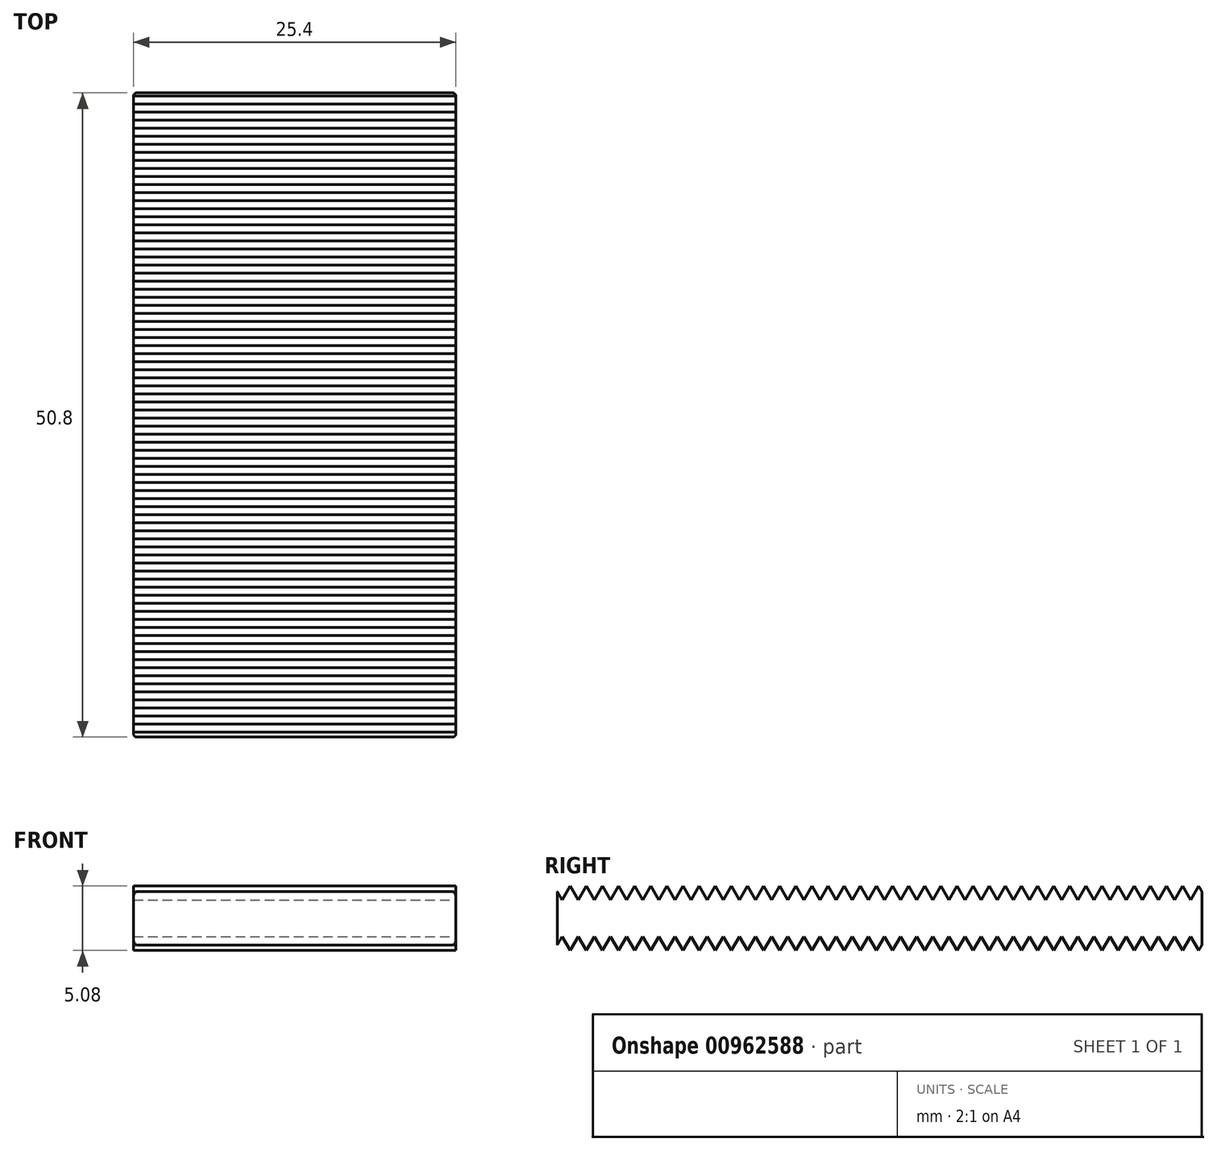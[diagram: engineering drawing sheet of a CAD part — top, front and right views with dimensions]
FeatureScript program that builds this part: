
annotation { "Feature Type Name" : "Feature", "Feature Type Description" : "" }
export const myFeature = defineFeature(function(context is Context, id is Id, definition is map)
    precondition{}
    {
        {
            var Q0;
            Q0=qCreatedBy(makeId("Front.planeOp"),FACE);
            var sketch = newSketch(context, id + "F0", { "sketchPlane" : qUnion([Q0])});
            skLineSegment(sketch, "E0.bottom", {"start": v(12.7, -2.54) * mm, "end": v(-12.7, -2.54) * mm});
            skLineSegment(sketch, "E0.top", {"start": v(12.7, 2.54) * mm, "end": v(-12.7, 2.54) * mm});
            skLineSegment(sketch, "E0.left", {"start": v(12.7, -2.54) * mm, "end": v(12.7, 2.54) * mm});
            skLineSegment(sketch, "E0.right", {"start": v(-12.7, -2.54) * mm, "end": v(-12.7, 2.54) * mm});
            skPoint(sketch, "E0.middle", {"position": v(0, 0) * mm});
            skSolve(sketch);
        }
        {
            var Q0;
            Q0=qSketchRegion(id+"F0",true);
            extrude(context, id + "F1", {"entities" : qUnion([Q0]), "endBound" : BoundingType.SYMMETRIC, "depth" : 50.8 * mm, "offsetDistance" : 25.4 * mm});
        }
        {
            var Q0;
            Q0=qCreatedBy(makeId("Right.planeOp"),FACE);
            var sketch = newSketch(context, id + "F2", { "sketchPlane" : qUnion([Q0])});
            skLineSegment(sketch, "E1", {"start": v(1.02, -2.54) * mm, "end": v(0.38, -1.44) * mm});
            skLineSegment(sketch, "E2", {"start": v(0.38, -1.44) * mm, "end": v(-0.25, -2.54) * mm});
            skLineSegment(sketch, "E3.1.0.0", {"start": v(2.29, -2.54) * mm, "end": v(1.65, -1.44) * mm});
            skLineSegment(sketch, "E3.1.0.1", {"start": v(1.65, -1.44) * mm, "end": v(1.02, -2.54) * mm});
            skLineSegment(sketch, "E3.2.0.0", {"start": v(3.56, -2.54) * mm, "end": v(2.92, -1.44) * mm});
            skLineSegment(sketch, "E3.2.0.1", {"start": v(2.92, -1.44) * mm, "end": v(2.29, -2.54) * mm});
            skLineSegment(sketch, "E3.3.0.0", {"start": v(4.83, -2.54) * mm, "end": v(4.2, -1.44) * mm});
            skLineSegment(sketch, "E3.3.0.1", {"start": v(4.2, -1.44) * mm, "end": v(3.56, -2.54) * mm});
            skLineSegment(sketch, "E3.4.0.0", {"start": v(6.1, -2.54) * mm, "end": v(5.46, -1.44) * mm});
            skLineSegment(sketch, "E3.4.0.1", {"start": v(5.46, -1.44) * mm, "end": v(4.83, -2.54) * mm});
            skLineSegment(sketch, "E3.5.0.0", {"start": v(7.37, -2.54) * mm, "end": v(6.73, -1.44) * mm});
            skLineSegment(sketch, "E3.5.0.1", {"start": v(6.73, -1.44) * mm, "end": v(6.1, -2.54) * mm});
            skLineSegment(sketch, "E3.6.0.0", {"start": v(8.64, -2.54) * mm, "end": v(8, -1.44) * mm});
            skLineSegment(sketch, "E3.6.0.1", {"start": v(8, -1.44) * mm, "end": v(7.37, -2.54) * mm});
            skLineSegment(sketch, "E3.7.0.0", {"start": v(9.9, -2.54) * mm, "end": v(9.27, -1.44) * mm});
            skLineSegment(sketch, "E3.7.0.1", {"start": v(9.27, -1.44) * mm, "end": v(8.64, -2.54) * mm});
            skLineSegment(sketch, "E3.8.0.0", {"start": v(11.18, -2.54) * mm, "end": v(10.54, -1.44) * mm});
            skLineSegment(sketch, "E3.8.0.1", {"start": v(10.54, -1.44) * mm, "end": v(9.9, -2.54) * mm});
            skLineSegment(sketch, "E3.9.0.0", {"start": v(12.45, -2.54) * mm, "end": v(11.81, -1.44) * mm});
            skLineSegment(sketch, "E3.9.0.1", {"start": v(11.81, -1.44) * mm, "end": v(11.18, -2.54) * mm});
            skLineSegment(sketch, "E3.10.0.0", {"start": v(13.72, -2.54) * mm, "end": v(13.08, -1.44) * mm});
            skLineSegment(sketch, "E3.10.0.1", {"start": v(13.08, -1.44) * mm, "end": v(12.45, -2.54) * mm});
            skLineSegment(sketch, "E3.11.0.0", {"start": v(14.99, -2.54) * mm, "end": v(14.35, -1.44) * mm});
            skLineSegment(sketch, "E3.11.0.1", {"start": v(14.35, -1.44) * mm, "end": v(13.72, -2.54) * mm});
            skLineSegment(sketch, "E3.12.0.0", {"start": v(16.26, -2.54) * mm, "end": v(15.62, -1.44) * mm});
            skLineSegment(sketch, "E3.12.0.1", {"start": v(15.62, -1.44) * mm, "end": v(14.99, -2.54) * mm});
            skLineSegment(sketch, "E3.13.0.0", {"start": v(17.53, -2.54) * mm, "end": v(16.9, -1.44) * mm});
            skLineSegment(sketch, "E3.13.0.1", {"start": v(16.9, -1.44) * mm, "end": v(16.26, -2.54) * mm});
            skLineSegment(sketch, "E3.14.0.0", {"start": v(18.8, -2.54) * mm, "end": v(18.16, -1.44) * mm});
            skLineSegment(sketch, "E3.14.0.1", {"start": v(18.16, -1.44) * mm, "end": v(17.53, -2.54) * mm});
            skLineSegment(sketch, "E3.15.0.0", {"start": v(20.07, -2.54) * mm, "end": v(19.43, -1.44) * mm});
            skLineSegment(sketch, "E3.15.0.1", {"start": v(19.43, -1.44) * mm, "end": v(18.8, -2.54) * mm});
            skLineSegment(sketch, "E3.16.0.0", {"start": v(21.34, -2.54) * mm, "end": v(20.7, -1.44) * mm});
            skLineSegment(sketch, "E3.16.0.1", {"start": v(20.7, -1.44) * mm, "end": v(20.07, -2.54) * mm});
            skLineSegment(sketch, "E3.17.0.0", {"start": v(22.6, -2.54) * mm, "end": v(21.97, -1.44) * mm});
            skLineSegment(sketch, "E3.17.0.1", {"start": v(21.97, -1.44) * mm, "end": v(21.34, -2.54) * mm});
            skLineSegment(sketch, "E3.18.0.0", {"start": v(23.88, -2.54) * mm, "end": v(23.24, -1.44) * mm});
            skLineSegment(sketch, "E3.18.0.1", {"start": v(23.24, -1.44) * mm, "end": v(22.6, -2.54) * mm});
            skLineSegment(sketch, "E3.19.0.0", {"start": v(25.15, -2.54) * mm, "end": v(24.51, -1.44) * mm});
            skLineSegment(sketch, "E3.19.0.1", {"start": v(24.51, -1.44) * mm, "end": v(23.88, -2.54) * mm});
            skLineSegment(sketch, "E3.20.0.0", {"start": v(26.42, -2.54) * mm, "end": v(25.78, -1.44) * mm});
            skLineSegment(sketch, "E3.20.0.1", {"start": v(25.78, -1.44) * mm, "end": v(25.15, -2.54) * mm});
            skLineSegment(sketch, "E3.21.0.0", {"start": v(27.69, -2.54) * mm, "end": v(27.05, -1.44) * mm});
            skLineSegment(sketch, "E3.21.0.1", {"start": v(27.05, -1.44) * mm, "end": v(26.42, -2.54) * mm});
            skLineSegment(sketch, "E3.22.0.0", {"start": v(28.96, -2.54) * mm, "end": v(28.32, -1.44) * mm});
            skLineSegment(sketch, "E3.22.0.1", {"start": v(28.32, -1.44) * mm, "end": v(27.69, -2.54) * mm});
            skLineSegment(sketch, "E3.23.0.0", {"start": v(30.23, -2.54) * mm, "end": v(29.6, -1.44) * mm});
            skLineSegment(sketch, "E3.23.0.1", {"start": v(29.6, -1.44) * mm, "end": v(28.96, -2.54) * mm});
            skLineSegment(sketch, "E3.24.0.0", {"start": v(31.5, -2.54) * mm, "end": v(30.86, -1.44) * mm});
            skLineSegment(sketch, "E3.24.0.1", {"start": v(30.86, -1.44) * mm, "end": v(30.23, -2.54) * mm});
            skLineSegment(sketch, "E3.direction1", {"start": v(-0.25, -2.54) * mm, "end": v(1.02, -2.54) * mm, "construction": true});
            skLineSegment(sketch, "E4.1.0.0", {"start": v(-0.25, -2.54) * mm, "end": v(-0.89, -1.44) * mm});
            skLineSegment(sketch, "E4.1.0.1", {"start": v(-0.89, -1.44) * mm, "end": v(-1.52, -2.54) * mm});
            skLineSegment(sketch, "E4.2.0.0", {"start": v(-1.52, -2.54) * mm, "end": v(-2.16, -1.44) * mm});
            skLineSegment(sketch, "E4.2.0.1", {"start": v(-2.16, -1.44) * mm, "end": v(-2.8, -2.54) * mm});
            skLineSegment(sketch, "E4.3.0.0", {"start": v(-2.8, -2.54) * mm, "end": v(-3.43, -1.44) * mm});
            skLineSegment(sketch, "E4.3.0.1", {"start": v(-3.43, -1.44) * mm, "end": v(-4.06, -2.54) * mm});
            skLineSegment(sketch, "E4.4.0.0", {"start": v(-4.06, -2.54) * mm, "end": v(-4.7, -1.44) * mm});
            skLineSegment(sketch, "E4.4.0.1", {"start": v(-4.7, -1.44) * mm, "end": v(-5.33, -2.54) * mm});
            skLineSegment(sketch, "E4.5.0.0", {"start": v(-5.33, -2.54) * mm, "end": v(-5.97, -1.44) * mm});
            skLineSegment(sketch, "E4.5.0.1", {"start": v(-5.97, -1.44) * mm, "end": v(-6.6, -2.54) * mm});
            skLineSegment(sketch, "E4.6.0.0", {"start": v(-6.6, -2.54) * mm, "end": v(-7.24, -1.44) * mm});
            skLineSegment(sketch, "E4.6.0.1", {"start": v(-7.24, -1.44) * mm, "end": v(-7.87, -2.54) * mm});
            skLineSegment(sketch, "E4.7.0.0", {"start": v(-7.87, -2.54) * mm, "end": v(-8.5, -1.44) * mm});
            skLineSegment(sketch, "E4.7.0.1", {"start": v(-8.5, -1.44) * mm, "end": v(-9.14, -2.54) * mm});
            skLineSegment(sketch, "E4.8.0.0", {"start": v(-9.14, -2.54) * mm, "end": v(-9.78, -1.44) * mm});
            skLineSegment(sketch, "E4.8.0.1", {"start": v(-9.78, -1.44) * mm, "end": v(-10.41, -2.54) * mm});
            skLineSegment(sketch, "E4.9.0.0", {"start": v(-10.41, -2.54) * mm, "end": v(-11.05, -1.44) * mm});
            skLineSegment(sketch, "E4.9.0.1", {"start": v(-11.05, -1.44) * mm, "end": v(-11.68, -2.54) * mm});
            skLineSegment(sketch, "E4.10.0.0", {"start": v(-11.68, -2.54) * mm, "end": v(-12.32, -1.44) * mm});
            skLineSegment(sketch, "E4.10.0.1", {"start": v(-12.32, -1.44) * mm, "end": v(-12.95, -2.54) * mm});
            skLineSegment(sketch, "E4.11.0.0", {"start": v(-12.95, -2.54) * mm, "end": v(-13.59, -1.44) * mm});
            skLineSegment(sketch, "E4.11.0.1", {"start": v(-13.59, -1.44) * mm, "end": v(-14.22, -2.54) * mm});
            skLineSegment(sketch, "E4.12.0.0", {"start": v(-14.22, -2.54) * mm, "end": v(-14.86, -1.44) * mm});
            skLineSegment(sketch, "E4.12.0.1", {"start": v(-14.86, -1.44) * mm, "end": v(-15.5, -2.54) * mm});
            skLineSegment(sketch, "E4.13.0.0", {"start": v(-15.5, -2.54) * mm, "end": v(-16.13, -1.44) * mm});
            skLineSegment(sketch, "E4.13.0.1", {"start": v(-16.13, -1.44) * mm, "end": v(-16.76, -2.54) * mm});
            skLineSegment(sketch, "E4.14.0.0", {"start": v(-16.76, -2.54) * mm, "end": v(-17.4, -1.44) * mm});
            skLineSegment(sketch, "E4.14.0.1", {"start": v(-17.4, -1.44) * mm, "end": v(-18.03, -2.54) * mm});
            skLineSegment(sketch, "E4.15.0.0", {"start": v(-18.03, -2.54) * mm, "end": v(-18.67, -1.44) * mm});
            skLineSegment(sketch, "E4.15.0.1", {"start": v(-18.67, -1.44) * mm, "end": v(-19.3, -2.54) * mm});
            skLineSegment(sketch, "E4.16.0.0", {"start": v(-19.3, -2.54) * mm, "end": v(-19.94, -1.44) * mm});
            skLineSegment(sketch, "E4.16.0.1", {"start": v(-19.94, -1.44) * mm, "end": v(-20.57, -2.54) * mm});
            skLineSegment(sketch, "E4.17.0.0", {"start": v(-20.57, -2.54) * mm, "end": v(-21.2, -1.44) * mm});
            skLineSegment(sketch, "E4.17.0.1", {"start": v(-21.2, -1.44) * mm, "end": v(-21.84, -2.54) * mm});
            skLineSegment(sketch, "E4.18.0.0", {"start": v(-21.84, -2.54) * mm, "end": v(-22.48, -1.44) * mm});
            skLineSegment(sketch, "E4.18.0.1", {"start": v(-22.48, -1.44) * mm, "end": v(-23.11, -2.54) * mm});
            skLineSegment(sketch, "E4.19.0.0", {"start": v(-23.11, -2.54) * mm, "end": v(-23.75, -1.44) * mm});
            skLineSegment(sketch, "E4.19.0.1", {"start": v(-23.75, -1.44) * mm, "end": v(-24.38, -2.54) * mm});
            skLineSegment(sketch, "E4.20.0.0", {"start": v(-24.38, -2.54) * mm, "end": v(-25.02, -1.44) * mm});
            skLineSegment(sketch, "E4.20.0.1", {"start": v(-25.02, -1.44) * mm, "end": v(-25.65, -2.54) * mm});
            skLineSegment(sketch, "E4.21.0.0", {"start": v(-25.65, -2.54) * mm, "end": v(-26.29, -1.44) * mm});
            skLineSegment(sketch, "E4.21.0.1", {"start": v(-26.29, -1.44) * mm, "end": v(-26.92, -2.54) * mm});
            skLineSegment(sketch, "E4.22.0.0", {"start": v(-26.92, -2.54) * mm, "end": v(-27.56, -1.44) * mm});
            skLineSegment(sketch, "E4.22.0.1", {"start": v(-27.56, -1.44) * mm, "end": v(-28.2, -2.54) * mm});
            skLineSegment(sketch, "E4.23.0.0", {"start": v(-28.2, -2.54) * mm, "end": v(-28.83, -1.44) * mm});
            skLineSegment(sketch, "E4.23.0.1", {"start": v(-28.83, -1.44) * mm, "end": v(-29.46, -2.54) * mm});
            skLineSegment(sketch, "E4.direction1", {"start": v(-0.25, -2.54) * mm, "end": v(-1.52, -2.54) * mm, "construction": true});
            skLineSegment(sketch, "E5", {"start": v(-29.46, -2.54) * mm, "end": v(-29.46, -2.8) * mm});
            skLineSegment(sketch, "E6", {"start": v(-29.46, -2.8) * mm, "end": v(31.5, -2.8) * mm});
            skLineSegment(sketch, "E7", {"start": v(31.5, -2.8) * mm, "end": v(31.5, -2.54) * mm});
            skLineSegment(sketch, "E8.MirrorCS", {"start": v(31.5, 2.8) * mm, "end": v(31.5, 2.54) * mm});
            skLineSegment(sketch, "E9.MirrorCS", {"start": v(-29.46, 2.54) * mm, "end": v(-29.46, 2.8) * mm});
            skLineSegment(sketch, "E10.MirrorCS", {"start": v(1.02, 2.54) * mm, "end": v(0.38, 1.44) * mm});
            skLineSegment(sketch, "E11.MirrorCS", {"start": v(-0.25, 2.54) * mm, "end": v(1.02, 2.54) * mm, "construction": true});
            skLineSegment(sketch, "E12.MirrorCS", {"start": v(1.65, 1.44) * mm, "end": v(1.02, 2.54) * mm});
            skLineSegment(sketch, "E13.MirrorCS", {"start": v(0.38, 1.44) * mm, "end": v(-0.25, 2.54) * mm});
            skLineSegment(sketch, "E14.MirrorCS", {"start": v(2.29, 2.54) * mm, "end": v(1.65, 1.44) * mm});
            skLineSegment(sketch, "E15.MirrorCS", {"start": v(-0.89, 1.44) * mm, "end": v(-1.52, 2.54) * mm});
            skLineSegment(sketch, "E16.MirrorCS", {"start": v(-0.25, 2.54) * mm, "end": v(-1.52, 2.54) * mm, "construction": true});
            skLineSegment(sketch, "E17.MirrorCS", {"start": v(-0.25, 2.54) * mm, "end": v(-0.89, 1.44) * mm});
            skLineSegment(sketch, "E18.MirrorCS", {"start": v(29.6, 1.44) * mm, "end": v(28.96, 2.54) * mm});
            skLineSegment(sketch, "E19.MirrorCS", {"start": v(15.62, 1.44) * mm, "end": v(14.99, 2.54) * mm});
            skLineSegment(sketch, "E20.MirrorCS", {"start": v(-26.29, 1.44) * mm, "end": v(-26.92, 2.54) * mm});
            skLineSegment(sketch, "E21.MirrorCS", {"start": v(4.2, 1.44) * mm, "end": v(3.56, 2.54) * mm});
            skLineSegment(sketch, "E22.MirrorCS", {"start": v(-23.11, 2.54) * mm, "end": v(-23.75, 1.44) * mm});
            skLineSegment(sketch, "E23.MirrorCS", {"start": v(-13.59, 1.44) * mm, "end": v(-14.22, 2.54) * mm});
            skLineSegment(sketch, "E24.MirrorCS", {"start": v(12.45, 2.54) * mm, "end": v(11.81, 1.44) * mm});
            skLineSegment(sketch, "E25.MirrorCS", {"start": v(27.05, 1.44) * mm, "end": v(26.42, 2.54) * mm});
            skLineSegment(sketch, "E26.MirrorCS", {"start": v(2.92, 1.44) * mm, "end": v(2.29, 2.54) * mm});
            skLineSegment(sketch, "E27.MirrorCS", {"start": v(-12.32, 1.44) * mm, "end": v(-12.95, 2.54) * mm});
            skLineSegment(sketch, "E28.MirrorCS", {"start": v(-4.7, 1.44) * mm, "end": v(-5.33, 2.54) * mm});
            skLineSegment(sketch, "E29.MirrorCS", {"start": v(-28.83, 1.44) * mm, "end": v(-29.46, 2.54) * mm});
            skLineSegment(sketch, "E30.MirrorCS", {"start": v(9.9, 2.54) * mm, "end": v(9.27, 1.44) * mm});
            skLineSegment(sketch, "E31.MirrorCS", {"start": v(-17.4, 1.44) * mm, "end": v(-18.03, 2.54) * mm});
            skLineSegment(sketch, "E32.MirrorCS", {"start": v(6.73, 1.44) * mm, "end": v(6.1, 2.54) * mm});
            skLineSegment(sketch, "E33.MirrorCS", {"start": v(-3.43, 1.44) * mm, "end": v(-4.06, 2.54) * mm});
            skLineSegment(sketch, "E34.MirrorCS", {"start": v(-9.78, 1.44) * mm, "end": v(-10.41, 2.54) * mm});
            skLineSegment(sketch, "E35.MirrorCS", {"start": v(4.83, 2.54) * mm, "end": v(4.2, 1.44) * mm});
            skLineSegment(sketch, "E36.MirrorCS", {"start": v(-7.24, 1.44) * mm, "end": v(-7.87, 2.54) * mm});
            skLineSegment(sketch, "E37.MirrorCS", {"start": v(-1.52, 2.54) * mm, "end": v(-2.16, 1.44) * mm});
            skLineSegment(sketch, "E38.MirrorCS", {"start": v(-8.5, 1.44) * mm, "end": v(-9.14, 2.54) * mm});
            skLineSegment(sketch, "E39.MirrorCS", {"start": v(-18.67, 1.44) * mm, "end": v(-19.3, 2.54) * mm});
            skLineSegment(sketch, "E40.MirrorCS", {"start": v(8.64, 2.54) * mm, "end": v(8, 1.44) * mm});
            skLineSegment(sketch, "E41.MirrorCS", {"start": v(14.99, 2.54) * mm, "end": v(14.35, 1.44) * mm});
            skLineSegment(sketch, "E42.MirrorCS", {"start": v(-6.6, 2.54) * mm, "end": v(-7.24, 1.44) * mm});
            skLineSegment(sketch, "E43.MirrorCS", {"start": v(-12.95, 2.54) * mm, "end": v(-13.59, 1.44) * mm});
            skLineSegment(sketch, "E44.MirrorCS", {"start": v(31.5, 2.54) * mm, "end": v(30.86, 1.44) * mm});
            skLineSegment(sketch, "E45.MirrorCS", {"start": v(20.7, 1.44) * mm, "end": v(20.07, 2.54) * mm});
            skLineSegment(sketch, "E46.MirrorCS", {"start": v(-24.38, 2.54) * mm, "end": v(-25.02, 1.44) * mm});
            skLineSegment(sketch, "E47.MirrorCS", {"start": v(16.9, 1.44) * mm, "end": v(16.26, 2.54) * mm});
            skLineSegment(sketch, "E48.MirrorCS", {"start": v(30.86, 1.44) * mm, "end": v(30.23, 2.54) * mm});
            skLineSegment(sketch, "E49.MirrorCS", {"start": v(-18.03, 2.54) * mm, "end": v(-18.67, 1.44) * mm});
            skLineSegment(sketch, "E50.MirrorCS", {"start": v(-15.5, 2.54) * mm, "end": v(-16.13, 1.44) * mm});
            skLineSegment(sketch, "E51.MirrorCS", {"start": v(13.72, 2.54) * mm, "end": v(13.08, 1.44) * mm});
            skLineSegment(sketch, "E52.MirrorCS", {"start": v(-22.48, 1.44) * mm, "end": v(-23.11, 2.54) * mm});
            skLineSegment(sketch, "E53.MirrorCS", {"start": v(-19.94, 1.44) * mm, "end": v(-20.57, 2.54) * mm});
            skLineSegment(sketch, "E54.MirrorCS", {"start": v(17.53, 2.54) * mm, "end": v(16.9, 1.44) * mm});
            skLineSegment(sketch, "E55.MirrorCS", {"start": v(-9.14, 2.54) * mm, "end": v(-9.78, 1.44) * mm});
            skLineSegment(sketch, "E56.MirrorCS", {"start": v(-10.41, 2.54) * mm, "end": v(-11.05, 1.44) * mm});
            skLineSegment(sketch, "E57.MirrorCS", {"start": v(-16.76, 2.54) * mm, "end": v(-17.4, 1.44) * mm});
            skLineSegment(sketch, "E58.MirrorCS", {"start": v(24.51, 1.44) * mm, "end": v(23.88, 2.54) * mm});
            skLineSegment(sketch, "E59.MirrorCS", {"start": v(13.08, 1.44) * mm, "end": v(12.45, 2.54) * mm});
            skLineSegment(sketch, "E60.MirrorCS", {"start": v(-2.16, 1.44) * mm, "end": v(-2.8, 2.54) * mm});
            skLineSegment(sketch, "E61.MirrorCS", {"start": v(-5.33, 2.54) * mm, "end": v(-5.97, 1.44) * mm});
            skLineSegment(sketch, "E62.MirrorCS", {"start": v(7.37, 2.54) * mm, "end": v(6.73, 1.44) * mm});
            skLineSegment(sketch, "E63.MirrorCS", {"start": v(-27.56, 1.44) * mm, "end": v(-28.2, 2.54) * mm});
            skLineSegment(sketch, "E64.MirrorCS", {"start": v(-23.75, 1.44) * mm, "end": v(-24.38, 2.54) * mm});
            skLineSegment(sketch, "E65.MirrorCS", {"start": v(16.26, 2.54) * mm, "end": v(15.62, 1.44) * mm});
            skLineSegment(sketch, "E66.MirrorCS", {"start": v(6.1, 2.54) * mm, "end": v(5.46, 1.44) * mm});
            skLineSegment(sketch, "E67.MirrorCS", {"start": v(-4.06, 2.54) * mm, "end": v(-4.7, 1.44) * mm});
            skLineSegment(sketch, "E68.MirrorCS", {"start": v(28.32, 1.44) * mm, "end": v(27.69, 2.54) * mm});
            skLineSegment(sketch, "E69.MirrorCS", {"start": v(11.81, 1.44) * mm, "end": v(11.18, 2.54) * mm});
            skLineSegment(sketch, "E70.MirrorCS", {"start": v(-2.8, 2.54) * mm, "end": v(-3.43, 1.44) * mm});
            skLineSegment(sketch, "E71.MirrorCS", {"start": v(-11.05, 1.44) * mm, "end": v(-11.68, 2.54) * mm});
            skLineSegment(sketch, "E72.MirrorCS", {"start": v(18.16, 1.44) * mm, "end": v(17.53, 2.54) * mm});
            skLineSegment(sketch, "E73.MirrorCS", {"start": v(5.46, 1.44) * mm, "end": v(4.83, 2.54) * mm});
            skLineSegment(sketch, "E74.MirrorCS", {"start": v(-16.13, 1.44) * mm, "end": v(-16.76, 2.54) * mm});
            skLineSegment(sketch, "E75.MirrorCS", {"start": v(10.54, 1.44) * mm, "end": v(9.9, 2.54) * mm});
            skLineSegment(sketch, "E76.MirrorCS", {"start": v(11.18, 2.54) * mm, "end": v(10.54, 1.44) * mm});
            skLineSegment(sketch, "E77.MirrorCS", {"start": v(-20.57, 2.54) * mm, "end": v(-21.2, 1.44) * mm});
            skLineSegment(sketch, "E78.MirrorCS", {"start": v(-21.2, 1.44) * mm, "end": v(-21.84, 2.54) * mm});
            skLineSegment(sketch, "E79.MirrorCS", {"start": v(-5.97, 1.44) * mm, "end": v(-6.6, 2.54) * mm});
            skLineSegment(sketch, "E80.MirrorCS", {"start": v(-28.2, 2.54) * mm, "end": v(-28.83, 1.44) * mm});
            skLineSegment(sketch, "E81.MirrorCS", {"start": v(-7.87, 2.54) * mm, "end": v(-8.5, 1.44) * mm});
            skLineSegment(sketch, "E82.MirrorCS", {"start": v(25.15, 2.54) * mm, "end": v(24.51, 1.44) * mm});
            skLineSegment(sketch, "E83.MirrorCS", {"start": v(3.56, 2.54) * mm, "end": v(2.92, 1.44) * mm});
            skLineSegment(sketch, "E84.MirrorCS", {"start": v(9.27, 1.44) * mm, "end": v(8.64, 2.54) * mm});
            skLineSegment(sketch, "E85.MirrorCS", {"start": v(-19.3, 2.54) * mm, "end": v(-19.94, 1.44) * mm});
            skLineSegment(sketch, "E86.MirrorCS", {"start": v(30.23, 2.54) * mm, "end": v(29.6, 1.44) * mm});
            skLineSegment(sketch, "E87.MirrorCS", {"start": v(18.8, 2.54) * mm, "end": v(18.16, 1.44) * mm});
            skLineSegment(sketch, "E88.MirrorCS", {"start": v(-11.68, 2.54) * mm, "end": v(-12.32, 1.44) * mm});
            skLineSegment(sketch, "E89.MirrorCS", {"start": v(21.97, 1.44) * mm, "end": v(21.34, 2.54) * mm});
            skLineSegment(sketch, "E90.MirrorCS", {"start": v(21.34, 2.54) * mm, "end": v(20.7, 1.44) * mm});
            skLineSegment(sketch, "E91.MirrorCS", {"start": v(20.07, 2.54) * mm, "end": v(19.43, 1.44) * mm});
            skLineSegment(sketch, "E92.MirrorCS", {"start": v(-29.46, 2.8) * mm, "end": v(31.5, 2.8) * mm});
            skLineSegment(sketch, "E93.MirrorCS", {"start": v(27.69, 2.54) * mm, "end": v(27.05, 1.44) * mm});
            skLineSegment(sketch, "E94.MirrorCS", {"start": v(-25.65, 2.54) * mm, "end": v(-26.29, 1.44) * mm});
            skLineSegment(sketch, "E95.MirrorCS", {"start": v(-14.22, 2.54) * mm, "end": v(-14.86, 1.44) * mm});
            skLineSegment(sketch, "E96.MirrorCS", {"start": v(-26.92, 2.54) * mm, "end": v(-27.56, 1.44) * mm});
            skLineSegment(sketch, "E97.MirrorCS", {"start": v(23.24, 1.44) * mm, "end": v(22.6, 2.54) * mm});
            skLineSegment(sketch, "E98.MirrorCS", {"start": v(26.42, 2.54) * mm, "end": v(25.78, 1.44) * mm});
            skLineSegment(sketch, "E99.MirrorCS", {"start": v(28.96, 2.54) * mm, "end": v(28.32, 1.44) * mm});
            skLineSegment(sketch, "E100.MirrorCS", {"start": v(19.43, 1.44) * mm, "end": v(18.8, 2.54) * mm});
            skLineSegment(sketch, "E101.MirrorCS", {"start": v(25.78, 1.44) * mm, "end": v(25.15, 2.54) * mm});
            skLineSegment(sketch, "E102.MirrorCS", {"start": v(8, 1.44) * mm, "end": v(7.37, 2.54) * mm});
            skLineSegment(sketch, "E103.MirrorCS", {"start": v(22.6, 2.54) * mm, "end": v(21.97, 1.44) * mm});
            skLineSegment(sketch, "E104.MirrorCS", {"start": v(14.35, 1.44) * mm, "end": v(13.72, 2.54) * mm});
            skLineSegment(sketch, "E105.MirrorCS", {"start": v(-21.84, 2.54) * mm, "end": v(-22.48, 1.44) * mm});
            skLineSegment(sketch, "E106.MirrorCS", {"start": v(-14.86, 1.44) * mm, "end": v(-15.5, 2.54) * mm});
            skLineSegment(sketch, "E107.MirrorCS", {"start": v(-25.02, 1.44) * mm, "end": v(-25.65, 2.54) * mm});
            skLineSegment(sketch, "E108.MirrorCS", {"start": v(23.88, 2.54) * mm, "end": v(23.24, 1.44) * mm});
            skSolve(sketch);
        }
        {
            var Q0;
            Q0=qSketchRegion(id+"F2",true);
            extrude(context, id + "F3", {"entities" : qUnion([Q0]), "operationType" : NewBodyOperationType.REMOVE, "endBound" : BoundingType.SYMMETRIC, "oppositeDirection" : true, "depth" : 25.4 * mm, "offsetDistance" : 25.4 * mm});
        }
        {
            var Q0;
            Q0=makeQuery(id+"F1.opExtrude","CAP_EDGE",EDGE,{"disambiguationData":[OSD([sQuery(id+"F0.wireOp",EDGE,"E0.left")])],"isStart":false});
            var Q1;
            Q1=makeQuery(id+"F1.opExtrude","CAP_EDGE",EDGE,{"disambiguationData":[OSD([sQuery(id+"F0.wireOp",EDGE,"E0.right")])],"isStart":false});
            var Q2;
            Q2=makeQuery(id+"F3.boolean.opBoolean","MERGE",EDGE,{"derivedFrom":[makeQuery(id+"F1.opExtrude","CAP_EDGE",EDGE,{"disambiguationData":[OSD([sQuery(id+"F0.wireOp",EDGE,"E0.top")])],"isStart":false})],"fromTools":[makeQuery(id+"F3.opExtrude","SWEPT_EDGE",EDGE,{"disambiguationData":[OSD([sQuery(id+"F2.wireOp",EDGE,"accb9737-dca4-4821-836c-b98c3f27e90128.MirrorCS"),sQuery(id+"F2.wireOp",EDGE,"accb9737-dca4-4821-836c-b98c3f27e901305.MirrorCS")])]})]});
            var Q3;
            Q3=makeQuery(id+"F3.boolean.opBoolean","MERGE",EDGE,{"derivedFrom":[makeQuery(id+"F1.opExtrude","CAP_EDGE",EDGE,{"disambiguationData":[OSD([sQuery(id+"F0.wireOp",EDGE,"E0.bottom")])],"isStart":false})],"fromTools":[makeQuery(id+"F3.opExtrude","SWEPT_EDGE",EDGE,{"disambiguationData":[OSD([sQuery(id+"F2.wireOp",EDGE,"E4.74.0.1"),sQuery(id+"F2.wireOp",EDGE,"E4.75.0.0")])]})]});
            var Q4;
            Q4=makeQuery(id+"F1.opExtrude","CAP_EDGE",EDGE,{"disambiguationData":[OSD([sQuery(id+"F0.wireOp",EDGE,"E0.right")])],"isStart":true});
            var Q5;
            Q5=makeQuery(id+"F3.boolean.opBoolean","MERGE",EDGE,{"derivedFrom":[makeQuery(id+"F1.opExtrude","CAP_EDGE",EDGE,{"disambiguationData":[OSD([sQuery(id+"F0.wireOp",EDGE,"E0.top")])],"isStart":true})],"fromTools":[makeQuery(id+"F3.opExtrude","SWEPT_EDGE",EDGE,{"disambiguationData":[OSD([sQuery(id+"F2.wireOp",EDGE,"accb9737-dca4-4821-836c-b98c3f27e901234.MirrorCS"),sQuery(id+"F2.wireOp",EDGE,"accb9737-dca4-4821-836c-b98c3f27e901281.MirrorCS")])]})]});
            var Q6;
            Q6=makeQuery(id+"F3.boolean.opBoolean","MERGE",EDGE,{"derivedFrom":[makeQuery(id+"F1.opExtrude","CAP_EDGE",EDGE,{"disambiguationData":[OSD([sQuery(id+"F0.wireOp",EDGE,"E0.bottom")])],"isStart":true})],"fromTools":[makeQuery(id+"F3.opExtrude","SWEPT_EDGE",EDGE,{"disambiguationData":[OSD([sQuery(id+"F2.wireOp",EDGE,"7466ea39-6cbc-46fd-bf35-4a40d964e960.0.75.0"),sQuery(id+"F2.wireOp",EDGE,"7466ea39-6cbc-46fd-bf35-4a40d964e960.3.76.0")])]})]});
            var Q7;
            Q7=makeQuery(id+"F1.opExtrude","CAP_FACE",FACE,{"disambiguationData":[OSD([sQuery(id+"F0.wireOp",EDGE,"E0.bottom"),sQuery(id+"F0.wireOp",EDGE,"E0.top"),sQuery(id+"F0.wireOp",EDGE,"E0.left"),sQuery(id+"F0.wireOp",EDGE,"E0.right")])],"isStart":true});
            fillet(context, id + "F4", {"entities" : qUnion([Q0, Q1, Q2, Q3, Q4, Q5, Q6, Q7]), "radius" : 0.25 * mm, "tangentPropagation" : true, "allowEdgeOverflow" : false});
        }
    });
